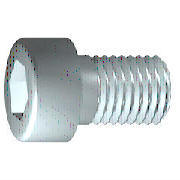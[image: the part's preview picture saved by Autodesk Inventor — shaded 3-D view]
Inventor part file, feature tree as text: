
AUTODESK INVENTOR PART (.ipt)
format: ipt  version: 2024 (Build 280153000, 153)  size: 192,000 bytes
history: native  units: mm (DEFAULTED — no unit token found)
features: other x1, extrude x1, plane x1, fillet x1
ambient origin geometry x7: Origin, YZ Plane, XY Plane, X Axis, Y Axis, Z Axis, Center Point
bodies: Solid1 (feature_tree)
feature tree (4):
  other  "Базовый элемент"
  extrude  "Паз"  Depth=14.25mm
  plane  "Work Plane1"
  fillet  "Fillet2"  Radius=0.429515mm
